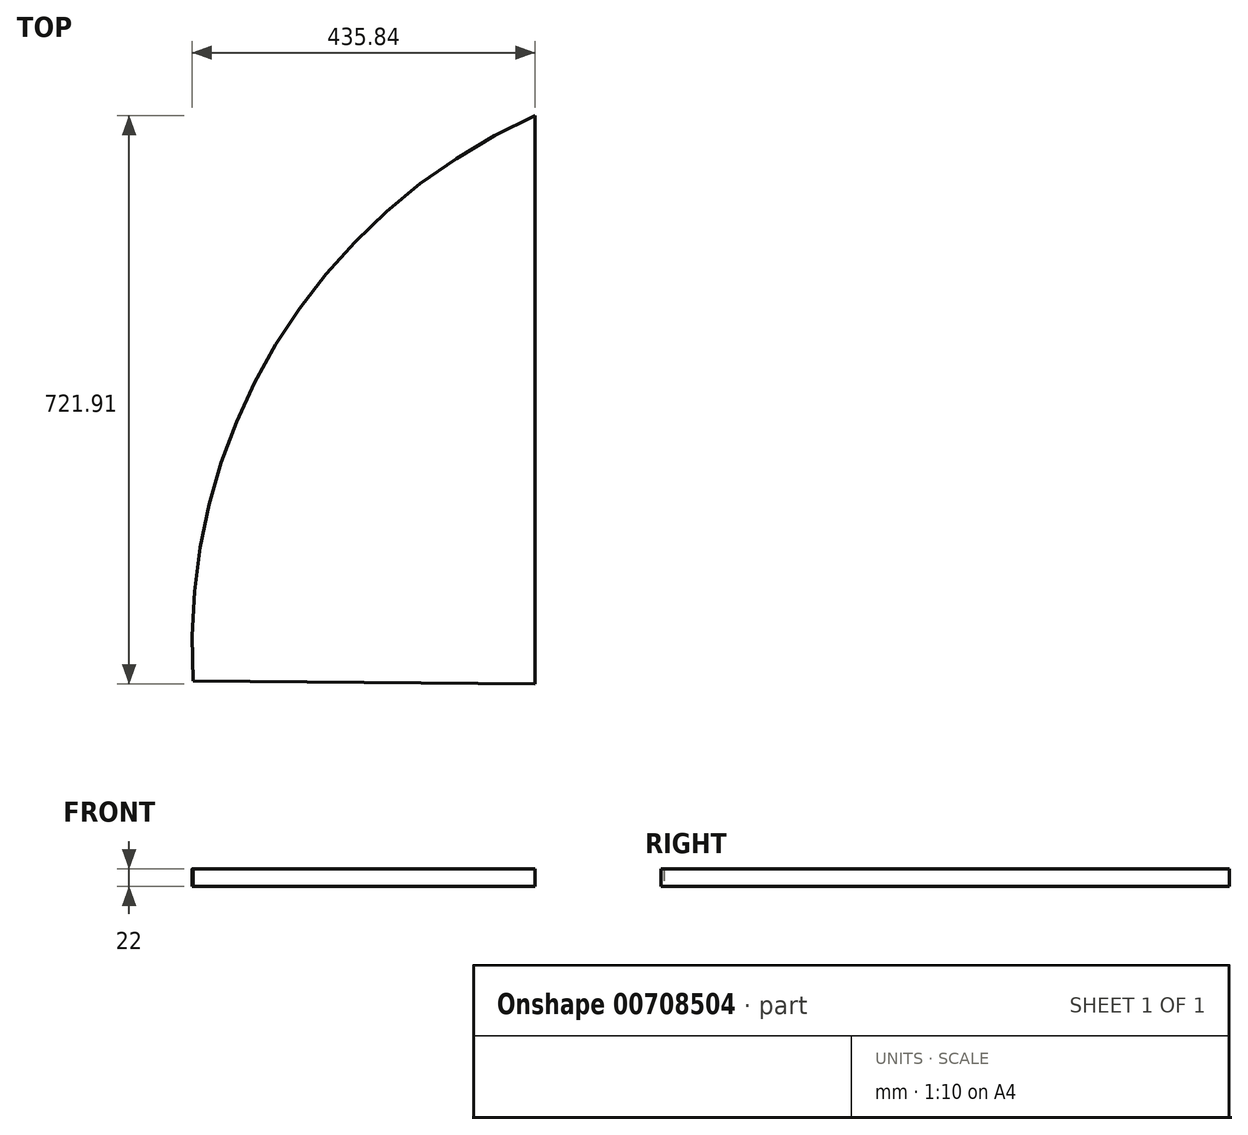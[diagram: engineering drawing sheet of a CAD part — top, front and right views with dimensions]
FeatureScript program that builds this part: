
annotation { "Feature Type Name" : "Feature", "Feature Type Description" : "" }
export const myFeature = defineFeature(function(context is Context, id is Id, definition is map)
    precondition{}
    {
        {
            var Q0;
            Q0=qCreatedBy(makeId("Top.planeOp"),FACE);
            var sketch = newSketch(context, id + "F0", { "sketchPlane" : qUnion([Q0])});
            skPoint(sketch, "E0.middle", {"position": v(0, 0) * mm});
            skPoint(sketch, "E1.end.orphan", {"position": v(-300, -300) * mm});
            skPoint(sketch, "E2.visualSharp", {"position": v(-300, 300) * mm});
            skPoint(sketch, "E3.visualSharp", {"position": v(-300, -52.1) * mm});
            skPoint(sketch, "E4.visualSharp", {"position": v(300, 300) * mm});
            skLineSegment(sketch, "E5", {"start": v(-300, -2.1) * mm, "end": v(-300, -2.1) * mm});
            skArc(sketch, "E6", {"start": v(-300, 671.9) * mm, "mid": v(-629.6, 380.88) * mm, "end": v(-734.4, -46.15) * mm});
            skPoint(sketch, "E7.visualSharp", {"position": v(-300, -74.1) * mm});
            skLineSegment(sketch, "E8", {"start": v(-300, 250) * mm, "end": v(-300, -50) * mm});
            skLineSegment(sketch, "E9", {"start": v(-300, -50) * mm, "end": v(-734.4, -46.15) * mm});
            skPoint(sketch, "E10.end.orphan", {"position": v(-732.48, -70.26) * mm});
            skPoint(sketch, "E11.orphan", {"position": v(-734.26, -48.26) * mm});
            skLineSegment(sketch, "E12", {"start": v(-300, 250) * mm, "end": v(-300, 671.9) * mm});
            skPoint(sketch, "E13.start.orphan", {"position": v(300, -300) * mm});
            skPoint(sketch, "E4.filletArc.start.orphan", {"position": v(300, 250) * mm});
            skSolve(sketch);
        }
        {
            var Q0;
            Q0=qSketchRegion(id+"F0",true);
            extrude(context, id + "F1", {"entities" : qUnion([Q0]), "depth" : 22 * mm, "offsetDistance" : 25 * mm});
        }
    });
